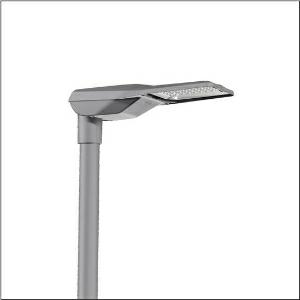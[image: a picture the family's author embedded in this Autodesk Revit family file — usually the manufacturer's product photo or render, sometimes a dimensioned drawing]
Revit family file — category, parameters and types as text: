
# Revit family: streetlight_sl_21_iq_mini___st1_0ab_5xe2m31g08hb_98c3
name_source: partatom
category: Lighting Fixtures
units: mm (PartAtom-declared; Revit-internal decimal feet)

## family parameters
Cut with Voids When Loaded = No
Host = Face
Light Source = No
Part Type = Normal
Room Calculation Point = No
Round Connector Dimension = Use Diameter
Shared = No

## types (1)
- --- (1 x LED, 8320 lm, 70.9 W, 3000K)
    Apparent Load = 71 VA
    CIE Flux Codes = 38 73 97 100 100
    Color Rendering = 70
    Color Temperature = 3000K
    Default Elevation = 1800 mm
    Description = Streetlight SL 21 iQ mini, mast luminaire, primary light control with lens, of PMMA, primary optical cover: cover, of toughened safety glass, transparent, light distribution: ST1.0aB, light emission: direct distribution, primary light characteristic: asymmetric, installation type: post-top, side-entry, LED, High Power LED, rated luminous flux: 8.320lm, luminous efficacy: 117lm/W, light colour: 730, colour temperature: 3000K, control gear: iQ Street-Remote, control: Street-Remote, Auto-Match, Temp-Guard, Lumen-Switch, Night-Set, Smart-Wire, Light-Fading, Desk-Remote (wireless, voltage-free reading and setting of iQ features in the workshop via application-optimized NFC function/RFID function), optimised constant luminous flux control (CLO 2.0), pre-setting: linear dimming characteristic, mains connection: 220..240V, AC, 50/60Hz, start of lifetime: 71W, end of service life: 75W, reduction: 31W, luminaire housing, of diecast aluminium, powder-coated, Siteco® metallic grey (DB 702S), corrosivity category C5 mid according to DIN EN ISO 12944, please order mast flange separately, inclination adjustable: 0°, 5°, 10°, 15°, sealing non-destructively replaceable, multi-level sealing system, length: 628mm, width: 235mm, height: 110mm, mast flange for spigot size: 42mm (side-entry): 5XC10008XM4, 60/48mm (side-entry/post-top): 5XC10108XM2, 76/60mm (side-entry/post-top): 5XC10108XM1, mounting height: 4..8m, protection rating (complete): IP66, insulation class (complete): insulation class II (safety insulation), certification: CE, ENEC, ENEC+, VDE, impact resistance: IK10, permissible operating ambient temperature for outdoor applications: -40..+50°C, standard-compliant lighting for roads and squares, packaging unit: 1 piece

Light Distribution: ST1.0aB
    Height = 110 mm
    Lamp = 1 x LED
    Lamp Light Flux = 8320 lm
    Lamp Power = 70.9 W
    Lamp count = 1
    Length = 625 mm
    Luminous efficacy = 117 lm/W
    Manufacturer = Siteco
    ModVariant = No
    Model = 5XE2M31G08HB
    Number of Poles = 1
    OnlyDefault = Yes
    Power Factor = 1
    Product Name = Streetlight SL 21 iQ mini | ST1.0aB
    Product group = mast luminaire | pylon top
    ProductGroupID = 6100
    Protection Class = Protection class II
    Protection Degree = IP 66
    RLX_Detail_Level = 1
    RLX_Emergency_Light_Flux = 0 lm
    RLX_Emergency_Type = 0
    RLX_Emergency_Type_DB = No
    RlxData = <blob elided: 26305 chars, md5=91a69df1>
    Socket = socket
    Standby Power = 0 W
    System Light Flux = 8320 lm
    System Power = 71 W
    Type Comments = factory setting: luminous flux: 100 % | dim-lin: 254 | 711 mA
    Type Image = l_1003519.jpg
    URL = http://relux.com
    VarID = @adj_157162
    Voltage = 0 V
    Weight = 0.00 kg
    Width = 234 mm

## geometry (parser evidence)
native form markers: Blend x4, Sweep x12
no freeform markers — native parametric forms only
